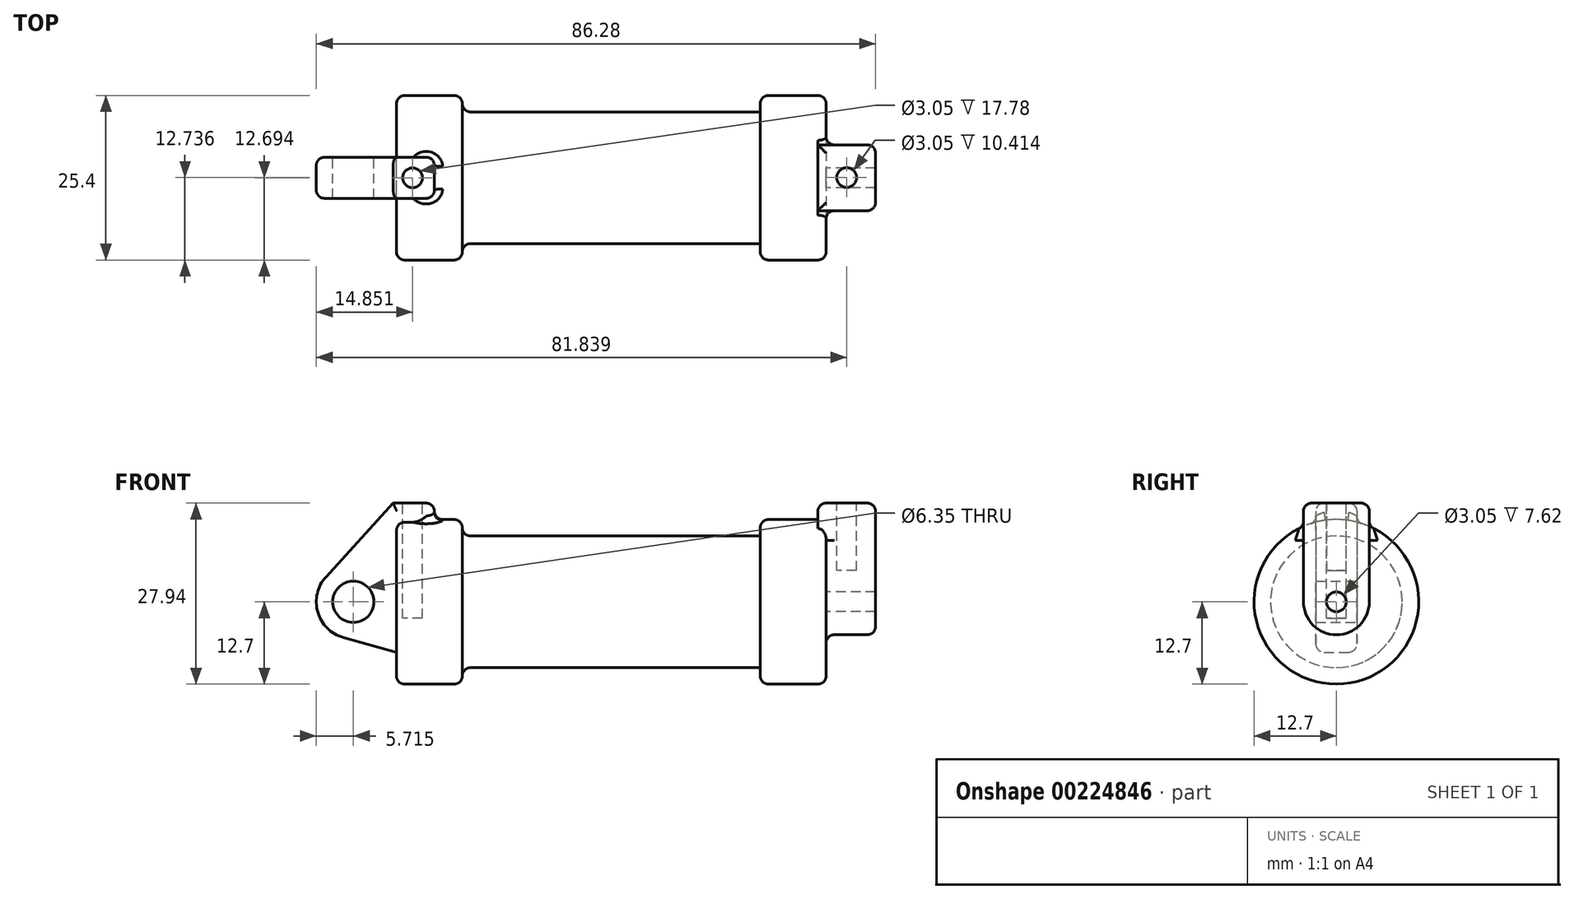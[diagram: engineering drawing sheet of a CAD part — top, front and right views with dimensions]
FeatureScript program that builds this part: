
annotation { "Feature Type Name" : "Feature", "Feature Type Description" : "" }
export const myFeature = defineFeature(function(context is Context, id is Id, definition is map)
    precondition{}
    {
        {
            var Q0;
            Q0=qCreatedBy(makeId("Front.planeOp"),FACE);
            var sketch = newSketch(context, id + "F0", { "sketchPlane" : qUnion([Q0])});
            skLineSegment(sketch, "E0", {"start": v(0, 0) * mm, "end": v(0, 12.7) * mm});
            skLineSegment(sketch, "E1", {"start": v(0, 12.7) * mm, "end": v(10.16, 12.7) * mm});
            skLineSegment(sketch, "E2", {"start": v(10.16, 12.7) * mm, "end": v(10.16, 10.16) * mm});
            skLineSegment(sketch, "E3", {"start": v(10.16, 10.16) * mm, "end": v(56.13, 10.16) * mm});
            skLineSegment(sketch, "E4", {"start": v(56.13, 10.16) * mm, "end": v(56.13, 12.7) * mm});
            skLineSegment(sketch, "E5", {"start": v(56.13, 12.7) * mm, "end": v(66.3, 12.7) * mm});
            skLineSegment(sketch, "E6", {"start": v(66.3, 12.7) * mm, "end": v(66.3, 0) * mm});
            skLineSegment(sketch, "E7", {"start": v(66.3, 0) * mm, "end": v(0, 0) * mm});
            skLineSegment(sketch, "E8", {"start": v(5.84, 15.24) * mm, "end": v(-0.5, 15.24) * mm});
            skLineSegment(sketch, "E9", {"start": v(-0.5, 15.24) * mm, "end": v(-10.88, 3.85) * mm});
            skLineSegment(sketch, "E10", {"start": v(0, 0) * mm, "end": v(-6.65, 0) * mm});
            skCircle(sketch, "E11", {"center": v(-6.65, 0) * mm, "radius": 5.72 * mm});
            skCircle(sketch, "E12", {"center": v(-6.65, 0) * mm, "radius": 3.18 * mm});
            skLineSegment(sketch, "E13", {"start": v(5.84, 15.24) * mm, "end": v(5.84, -9.4) * mm});
            skLineSegment(sketch, "E14", {"start": v(5.84, -9.4) * mm, "end": v(-8.18, -5.5) * mm});
            skSolve(sketch);
        }
        {
            var Q0;
            {var subQ0=sQuery(id+"F0.wireOp",EDGE,"E2");Q0=makeQuery(id+"F0.imprint","IMPRINT",FACE,{"disambiguationData":[TD([[makeQuery(id+"F0.imprint","IMPRINT",EDGE,{"derivedFrom":subQ0}),-1.0]])]});}
            var Q1;
            {var subQ0=sQuery(id+"F0.wireOp",EDGE,"E0");Q1=makeQuery(id+"F0.imprint","IMPRINT",FACE,{"disambiguationData":[TD([[makeQuery(id+"F0.imprint","IMPRINT",EDGE,{"derivedFrom":subQ0}),-1.0]])]});}
            var Q2;
            Q2=sQuery(id+"F0.wireOp",EDGE,"E7");
            revolve(context, id + "F1", {"entities" : qUnion([Q0, Q1]), "axis" : qUnion([Q2]), "revolveType" : RevolveType.FULL});
        }
        {
            var Q0;
            {var subQ3=sQuery(id+"F0.wireOp",EDGE,"E0");Q0=makeQuery(id+"F0.imprint","IMPRINT",FACE,{"disambiguationData":[TD([[makeQuery(id+"F0.imprint","IMPRINT",EDGE,{"derivedFrom":subQ3}),1.0]])]});}
            var Q1;
            {var subQ4=sQuery(id+"F0.wireOp",EDGE,"E12");Q1=makeQuery(id+"F0.imprint","IMPRINT",FACE,{"disambiguationData":[TD([[makeQuery(id+"F0.imprint","IMPRINT",EDGE,{"derivedFrom":subQ4}),-1.0]])]});}
            var Q2;
            {var subQ0=sQuery(id+"F0.wireOp",EDGE,"E14");Q2=makeQuery(id+"F0.imprint","IMPRINT",FACE,{"disambiguationData":[TD([[makeQuery(id+"F0.imprint","IMPRINT",EDGE,{"derivedFrom":subQ0}),-1.0]])]});}
            var Q3;
            {var subQ0=sQuery(id+"F0.wireOp",EDGE,"E0");Q3=makeQuery(id+"F0.imprint","IMPRINT",FACE,{"disambiguationData":[TD([[makeQuery(id+"F0.imprint","IMPRINT",EDGE,{"derivedFrom":subQ0}),-1.0]])]});}
            var Q4;
            Q4=sQuery(id+"F0.wireOp",EDGE,"E1");
            extrude(context, id + "F2", {"entities" : qUnion([Q0, Q1, Q2, Q3]), "operationType" : NewBodyOperationType.ADD, "surfaceEntities" : qUnion([Q4]), "depth" : 6.35 * mm, "symmetric" : true});
        }
        {
            var Q0;
            Q0=makeQuery(id+"F2.opExtrude","SWEPT_FACE",FACE,{"disambiguationData":[OSD([sQuery(id+"F0.wireOp",EDGE,"E8")])]});
            var sketch = newSketch(context, id + "F3", { "sketchPlane" : qUnion([Q0])});
            skCircle(sketch, "E15", {"center": v(2.48, 0) * mm, "radius": 1.52 * mm});
            skSolve(sketch);
        }
        {
            var Q0;
            Q0 = qSketchRegion(id + "F3", true);
            extrude(context, id + "F4", {"entities" : qUnion([Q0]), "operationType" : NewBodyOperationType.REMOVE, "oppositeDirection" : true, "depth" : 17.78 * mm});
        }
        {
            var Q0;
            Q0=makeQuery(id+"F1.opRevolve","SWEPT_FACE",FACE,{"disambiguationData":[OSD([sQuery(id+"F0.wireOp",EDGE,"E6")])]});
            var sketch = newSketch(context, id + "F5", { "sketchPlane" : qUnion([Q0])});
            skCircle(sketch, "E16", {"center": v(0, 0) * mm, "radius": 5.08 * mm});
            skCircle(sketch, "E17", {"center": v(0, 0) * mm, "radius": 1.52 * mm});
            skLineSegment(sketch, "E18", {"start": v(-5.08, 0) * mm, "end": v(-5.08, 15.24) * mm});
            skLineSegment(sketch, "E19", {"start": v(5.08, 0) * mm, "end": v(5.08, 15.24) * mm});
            skLineSegment(sketch, "E20", {"start": v(-5.08, 15.24) * mm, "end": v(5.08, 15.24) * mm});
            skSolve(sketch);
        }
        {
            var Q0;
            {var subQ0=sQuery(id+"F5.wireOp",EDGE,"E20");Q0=makeQuery(id+"F5.imprint","IMPRINT",FACE,{"disambiguationData":[TD([[makeQuery(id+"F5.imprint","IMPRINT",EDGE,{"derivedFrom":subQ0}),-1.0]])]});}
            var Q1;
            {var subQ0=sQuery(id+"F5.wireOp",EDGE,"E18");var subQ1=sQuery(id+"F5.wireOp",EDGE,"E16");var subQ2=makeQuery(id+"F5.imprint","INTERSECT",VERTEX,{"derivedFrom":[subQ1,subQ0]});Q1=makeQuery(id+"F5.imprint","IMPRINT",FACE,{"disambiguationData":[TD([[makeQuery(id+"F5.imprint","IMPRINT",EDGE,{"disambiguationData":[TD([[subQ2,1.0]])],"derivedFrom":subQ1}),-1.0]])]});}
            var Q2;
            Q2=makeQuery(id+"F5.imprint","IMPRINT",FACE,{"disambiguationData":[TD([[makeQuery(id+"F5.imprint","IMPRINT",EDGE,{"derivedFrom":sQuery(id+"F5.wireOp",EDGE,"E17")}),-1.0]])]});
            extrude(context, id + "F6", {"entities" : qUnion([Q0, Q1, Q2]), "operationType" : NewBodyOperationType.ADD, "depth" : 7.62 * mm});
        }
        {
            var Q0;
            Q0=makeQuery(id+"F6.opExtrude","CAP_FACE",FACE,{"disambiguationData":[OSD([sQuery(id+"F5.wireOp",EDGE,"E16"),sQuery(id+"F5.wireOp",EDGE,"E17"),sQuery(id+"F5.wireOp",EDGE,"E18"),sQuery(id+"F5.wireOp",EDGE,"E19"),sQuery(id+"F5.wireOp",EDGE,"E20")])],"isStart":true});
            extrude(context, id + "F7", {"entities" : qUnion([Q0]), "operationType" : NewBodyOperationType.ADD, "depth" : 1.27 * mm});
        }
        {
            var Q0;
            {var subQ0=sQuery(id+"F5.wireOp",EDGE,"E20");Q0=makeQuery(id+"F7.boolean.opBoolean","MERGE",FACE,{"derivedFrom":[makeQuery(id+"F6.opExtrude","SWEPT_FACE",FACE,{"disambiguationData":[OSD([subQ0])]}),makeQuery(id+"F7.opExtrude","SWEPT_FACE",FACE,{"disambiguationData":[OSD([subQ0])]})]});}
            var sketch = newSketch(context, id + "F8", { "sketchPlane" : qUnion([Q0])});
            skCircle(sketch, "E21", {"center": v(69.47, 0.04) * mm, "radius": 1.52 * mm});
            skPoint(sketch, "E21.centerSnap0", {"position": v(69.47, -5.08) * mm});
            skSolve(sketch);
        }
        {
            var Q0;
            Q0=makeQuery(id+"F8.imprint","IMPRINT",FACE,{"disambiguationData":[TD([[makeQuery(id+"F8.imprint","IMPRINT",EDGE,{"derivedFrom":sQuery(id+"F8.wireOp",EDGE,"E21")}),1.0]])]});
            extrude(context, id + "F9", {"entities" : qUnion([Q0]), "operationType" : NewBodyOperationType.REMOVE, "oppositeDirection" : true, "depth" : 10.4 * mm});
        }
        {
            var Q0;
            Q0=makeQuery(id+"F1.opRevolve","SWEPT_EDGE",EDGE,{"disambiguationData":[OSD([sQuery(id+"F0.wireOp",EDGE,"E1"),sQuery(id+"F0.wireOp",EDGE,"E2")])]});
            var Q1;
            Q1=makeQuery(id+"F1.opRevolve","SWEPT_EDGE",EDGE,{"disambiguationData":[OSD([sQuery(id+"F0.wireOp",EDGE,"E2"),sQuery(id+"F0.wireOp",EDGE,"E3")])]});
            var Q2;
            Q2=makeQuery(id+"F1.opRevolve","SWEPT_EDGE",EDGE,{"disambiguationData":[OSD([sQuery(id+"F0.wireOp",EDGE,"E4"),sQuery(id+"F0.wireOp",EDGE,"E5")])]});
            var Q3;
            Q3=makeQuery(id+"F6.boolean.opBoolean","SPLIT",EDGE,{"disambiguationData":[OD(1.0)],"derivedFrom":makeQuery(id+"F1.opRevolve","SWEPT_EDGE",EDGE,{"disambiguationData":[OSD([sQuery(id+"F0.wireOp",EDGE,"E5"),sQuery(id+"F0.wireOp",EDGE,"E6")])]})});
            var Q4;
            Q4=makeQuery(id+"F1.opRevolve","SWEPT_EDGE",EDGE,{"disambiguationData":[OSD([sQuery(id+"F0.wireOp",EDGE,"E0"),sQuery(id+"F0.wireOp",EDGE,"E1")])]});
            fillet(context, id + "F10", {"entities" : qUnion([Q0, Q1, Q2, Q3, Q4]), "radius" : 1.27 * mm, "tangentPropagation" : true, "allowEdgeOverflow" : false});
        }
        {
            var Q0;
            Q0=makeQuery(id+"F2.opExtrude","CAP_EDGE",EDGE,{"disambiguationData":[OSD([sQuery(id+"F0.wireOp",EDGE,"E9")])],"isStart":false});
            var Q1;
            Q1=makeQuery(id+"F2.opExtrude","CAP_EDGE",EDGE,{"disambiguationData":[OSD([sQuery(id+"F0.wireOp",EDGE,"E9")])],"isStart":true});
            var Q2;
            Q2=makeQuery(id+"F2.opExtrude","SWEPT_FACE",FACE,{"disambiguationData":[OSD([sQuery(id+"F0.wireOp",EDGE,"E13")])]});
            var Q3;
            Q3=makeQuery(id+"F2.opExtrude","CAP_EDGE",EDGE,{"disambiguationData":[OSD([sQuery(id+"F0.wireOp",EDGE,"E8")])],"isStart":false});
            var Q4;
            Q4=makeQuery(id+"F2.opExtrude","CAP_EDGE",EDGE,{"disambiguationData":[OSD([sQuery(id+"F0.wireOp",EDGE,"E8")])],"isStart":true});
            fillet(context, id + "F11", {"entities" : qUnion([Q0, Q1, Q2, Q3, Q4]), "radius" : 1.27 * mm, "tangentPropagation" : true, "allowEdgeOverflow" : false});
        }
        {
            var Q0;
            {var subQ0=sQuery(id+"F5.wireOp",EDGE,"E18");Q0=makeQuery(id+"F10.opFillet","BLEND_EDGE",EDGE,{"blendedFrom":[makeQuery(id+"F6.boolean.opBoolean","SPLIT",EDGE,{"disambiguationData":[OD(1.0)],"derivedFrom":makeQuery(id+"F1.opRevolve","SWEPT_EDGE",EDGE,{"disambiguationData":[OSD([sQuery(id+"F0.wireOp",EDGE,"E5"),sQuery(id+"F0.wireOp",EDGE,"E6")])]})}),makeQuery(id+"F7.boolean.opBoolean","MERGE",FACE,{"derivedFrom":[makeQuery(id+"F6.opExtrude","SWEPT_FACE",FACE,{"disambiguationData":[OSD([subQ0])]}),makeQuery(id+"F7.opExtrude","SWEPT_FACE",FACE,{"disambiguationData":[OSD([subQ0])]})]})],"blendedInto":[makeQuery(id+"F7.boolean.opBoolean","MERGE",FACE,{"derivedFrom":[makeQuery(id+"F6.opExtrude","SWEPT_FACE",FACE,{"disambiguationData":[OSD([subQ0])]}),makeQuery(id+"F7.opExtrude","SWEPT_FACE",FACE,{"disambiguationData":[OSD([subQ0])]})]})]});}
            var Q1;
            {var subQ0=sQuery(id+"F5.wireOp",EDGE,"E20");var subQ1=sQuery(id+"F5.wireOp",EDGE,"E18");Q1=makeQuery(id+"F7.boolean.opBoolean","MERGE",EDGE,{"derivedFrom":[makeQuery(id+"F6.opExtrude","SWEPT_EDGE",EDGE,{"disambiguationData":[OSD([subQ1,subQ0])]}),makeQuery(id+"F7.opExtrude","SWEPT_EDGE",EDGE,{"disambiguationData":[OSD([subQ1,subQ0])]})]});}
            var Q2;
            Q2=makeQuery(id+"F7.opExtrude","CAP_EDGE",EDGE,{"disambiguationData":[OSD([sQuery(id+"F5.wireOp",EDGE,"E20")])],"isStart":false});
            var Q3;
            {var subQ0=sQuery(id+"F5.wireOp",EDGE,"E20");var subQ1=sQuery(id+"F5.wireOp",EDGE,"E19");Q3=makeQuery(id+"F7.boolean.opBoolean","MERGE",EDGE,{"derivedFrom":[makeQuery(id+"F6.opExtrude","SWEPT_EDGE",EDGE,{"disambiguationData":[OSD([subQ1,subQ0])]}),makeQuery(id+"F7.opExtrude","SWEPT_EDGE",EDGE,{"disambiguationData":[OSD([subQ1,subQ0])]})]});}
            var Q4;
            Q4=makeQuery(id+"F6.opExtrude","CAP_EDGE",EDGE,{"disambiguationData":[OSD([sQuery(id+"F5.wireOp",EDGE,"E20")])],"isStart":false});
            var Q5;
            Q5=makeQuery(id+"F6.opExtrude","CAP_EDGE",EDGE,{"disambiguationData":[OSD([sQuery(id+"F5.wireOp",EDGE,"E18")])],"isStart":false});
            fillet(context, id + "F12", {"entities" : qUnion([Q0, Q1, Q2, Q3, Q4, Q5]), "radius" : 1.27 * mm, "tangentPropagation" : true, "allowEdgeOverflow" : false});
        }
    });
